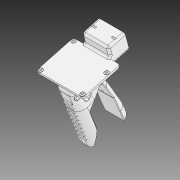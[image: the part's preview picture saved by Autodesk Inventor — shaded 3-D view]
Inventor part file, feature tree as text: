
AUTODESK INVENTOR PART (.ipt)
format: ipt  version: 2020 (Build 240168000, 168)  size: 2,270,208 bytes
history: native  units: in
note: dims shown in document units (in); Inventor stores cm internally (conversion verified against a paired STEP export)
features: sketch x23, extrude x22, fillet x8, projected_geometry x4, other x3, plane x3, chamfer x3, mirror x1, imported_body x1
ambient origin geometry x8: Origin, YZ Plane, XZ Plane, XY Plane, X Axis, Y Axis, Z Axis, Center Point
bodies: Solid1 (feature_tree)
feature tree (68):
  other  "Blocks"
  extrude  "Extrusion1"  Depth=0.1575in
  extrude  "Extrusion4"  Depth=0.3937in TaperAngle=0.0deg
  fillet  "Fillet1"  Radius=0.1378in
  extrude  "Extrusion5"  Depth=0.5906in
  extrude  "Extrusion6"  Depth=0.5906in TaperAngle=0.0deg
  plane  "Work Plane1"
  extrude  "Extrusion7"  Depth=0.2244in
  extrude  "Extrusion8"  Depth=0.2062in TaperAngle=0.0deg
  extrude  "Extrusion9"  Depth=0.3937in
  fillet  "Fillet2"  Radius=0.2062in
  chamfer  "Chamfer1"  Distance=0.2062in
  extrude  "Extrusion10"  TaperAngle=0.0deg  [1 undecoded]
  extrude  "Extrusion11"  Depth=0.3937in
  fillet  "Fillet3"  Radius=0.3937in
  extrude  "Extrusion12"  Depth=1.5in TaperAngle=0.0deg
  fillet  "Fillet4"  Radius=1.4001in
  extrude  "Extrusion13"  Depth=0.1181in TaperAngle=0.0deg
  plane  "Work Plane2"
  extrude  "Extrusion15"  Depth=0.4724in
  extrude  "Extrusion16"  Depth=0.5906in
  mirror  "Mirror1"
  fillet  "Fillet5"  Radius=0.5906in
  extrude  "Extrusion17"  Depth=0.1181in
  extrude  "Extrusion18"  TaperAngle=0.0deg  [1 undecoded]
  fillet  "Fillet6"  Radius=0.3937in
  sketch  "Sketch21"  dims[d62=75.0deg d63=0.0in d64=0.0in d65=0.3937in d66=0.0in]
  extrude  "Extrusion19"  [1 undecoded]
  extrude  "Extrusion20"  Depth=0.2244in
  extrude  "Extrusion21"  Depth=0.5906in TaperAngle=0.0deg
  plane  "Work Plane3"
  extrude  "Extrusion22"  Depth=0.1181in TaperAngle=45.0deg
  extrude  "Extrusion23"  Depth=0.0394in
  chamfer  "Chamfer2"  Distance=0.1181in
  extrude  "Extrusion24"  Depth=0.0591in TaperAngle=0.0deg
  extrude  "Extrusion25"  Depth=0.1181in
  chamfer  "Chamfer3"  Distance=0.1181in
  fillet  "Fillet7"  Radius=0.1181in
  fillet  "Fillet8"  [1 undecoded]
  sketch  "Sketch1"  dims[d0=0.0in d1=0.0in d2=0.1575in]
  sketch  "Sketch5"  dims[d7=3.3563in d8=0.0in d9=0.3937in d10=0.0in d11=0.1378in]
  sketch  "Sketch6"  dims[d12=1.1024in d13=0.5906in]
  sketch  "Sketch7"  dims[d14=0.4724in d15=0.5906in d16=0.0in]
  sketch  "Sketch8"  dims[d17=-0.3937in d18=0.2244in]
  sketch  "Sketch9"  dims[d19=0.1024in d20=0.0in d21=0.2062in d22=0.0in]
  sketch  "Sketch10"  dims[d23=0.3937in d24=0.0in d25=0.0787in]
  sketch  "Sketch11"  dims[d26=0.0276in d27=0.0787in d28=45.0deg d29=0.2062in d30=0.0in d31=0.2062in d32=0.0in]
  projected_geometry  "Projected Loop2"
  sketch  "Sketch12"  dims[d33=0.0315in d34=0.0in d35=0.0in]
  sketch  "Sketch13"  dims[d36=0.1969in d37=0.9687in d38=0.3937in]
  sketch  "Sketch14"  dims[d40=1.5in d41=0.0in d47=3.0907in d48=0.0in d49=1.4001in d50=0.0in]
  sketch  "Sketch17"  dims[d51=0.1181in d52=1.378in d53=0.0in]
  sketch  "Sketch18"  dims[d54=0.1378in d55=0.4724in]
  projected_geometry  "Projected Loop4"
  sketch  "Sketch19"  dims[d56=1.1024in d57=0.5906in d58=0.5906in d59=0.0in]
  sketch  "Sketch20"  dims[d60=0.1181in d61=0.1969in]
  projected_geometry  "Projected Loop6"
  sketch  "Sketch22"  dims[d67=0.3937in d68=0.0in d69=-0.3937in]
  sketch  "Sketch23"  dims[d70=0.2244in d71=0.2244in]
  sketch  "Sketch24"  dims[d72=0.1024in d73=0.0in d74=0.5906in d75=0.0in]
  projected_geometry  "Projected Loop7"
  sketch  "Sketch25"  dims[d76=0.9843in d77=0.1181in d78=0.0787in d79=45.0deg]
  sketch  "Sketch27"  dims[d80=2.3425in d81=2.6181in d82=2.1575in d83=1.9094in d84=0.6299in d85=0.1063in d86=0.0394in d87=0.1181in d88=0.0in]
  sketch  "Sketch28"  dims[d89=0.2362in d90=0.0591in d91=0.0in]
  other  "Block1"
  sketch  "Sketch29"  dims[d92=0.0394in d93=0.0787in d94=45.0deg d95=0.1181in d96=0.1181in d97=0.1181in]
  imported_body  "Base1"
  other  "Block1:1"
note: 4 required parameter values undecoded (feature->parameter linkage not recoverable at this tier; creation-order binding heuristic only, values carry confidence <= 0.55)
